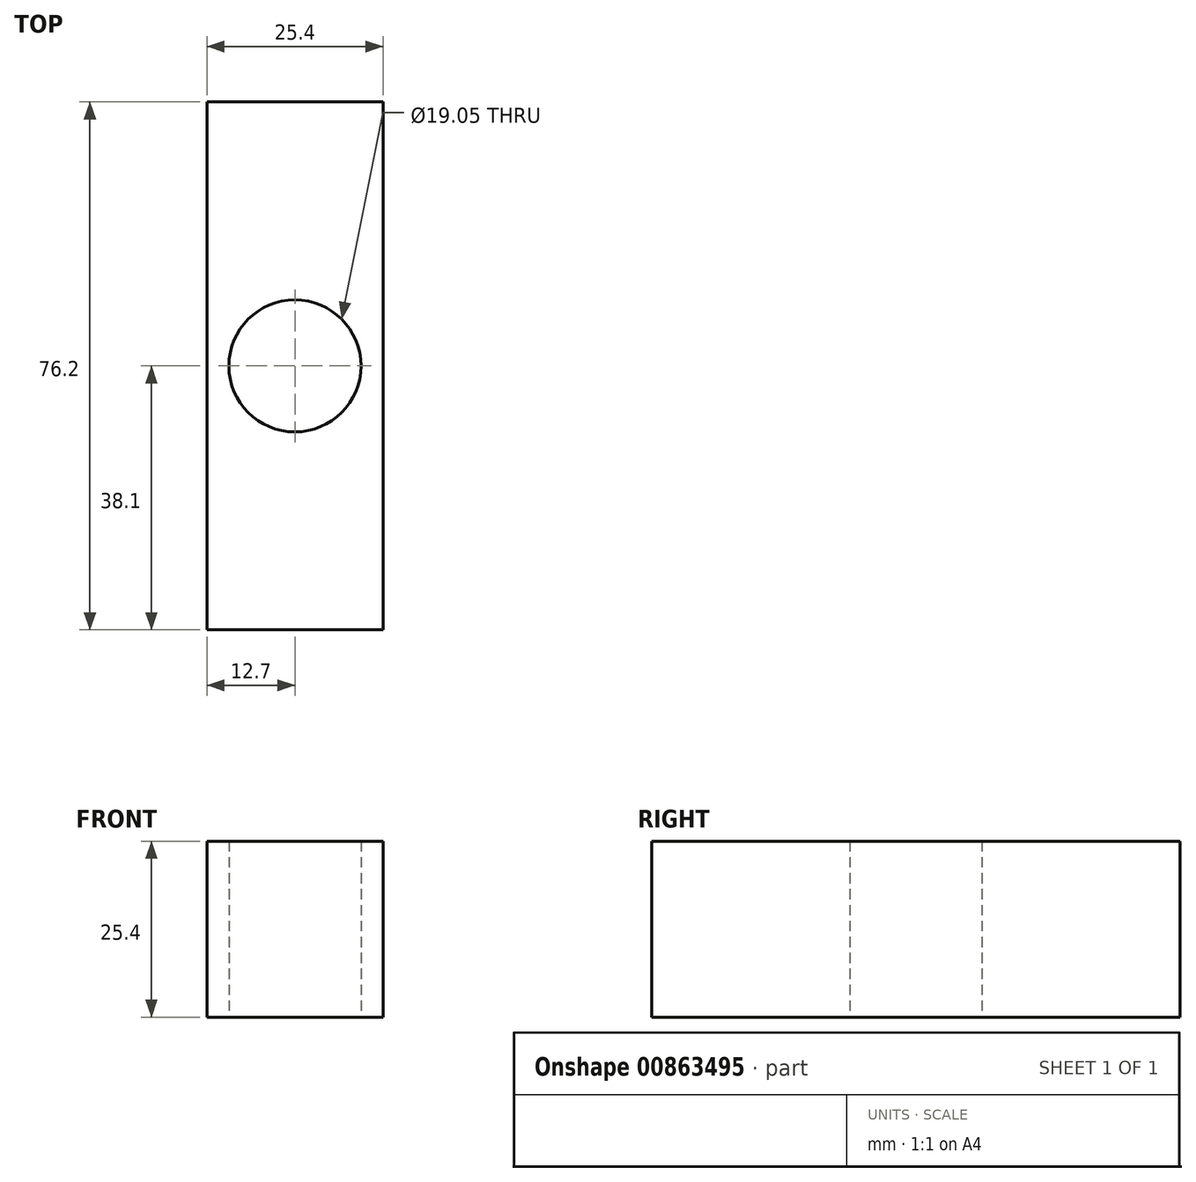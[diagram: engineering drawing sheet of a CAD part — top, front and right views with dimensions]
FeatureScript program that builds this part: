
annotation { "Feature Type Name" : "Feature", "Feature Type Description" : "" }
export const myFeature = defineFeature(function(context is Context, id is Id, definition is map)
    precondition{}
    {
        {
            var Q0;
            Q0=qCreatedBy(makeId("Top.planeOp"),FACE);
            var sketch = newSketch(context, id + "F0", { "sketchPlane" : qUnion([Q0])});
            skLineSegment(sketch, "E0.bottom", {"start": v(12.7, 38.1) * mm, "end": v(-12.7, 38.1) * mm});
            skLineSegment(sketch, "E0.top", {"start": v(12.7, -38.1) * mm, "end": v(-12.7, -38.1) * mm});
            skLineSegment(sketch, "E0.left", {"start": v(12.7, 38.1) * mm, "end": v(12.7, -38.1) * mm});
            skLineSegment(sketch, "E0.right", {"start": v(-12.7, 38.1) * mm, "end": v(-12.7, -38.1) * mm});
            skPoint(sketch, "E0.middle", {"position": v(0, 0) * mm});
            skCircle(sketch, "E1", {"center": v(0, 0) * mm, "radius": 9.53 * mm});
            skSolve(sketch);
        }
        {
            var Q0;
            Q0 = qSketchRegion(id + "F0", true);
            extrude(context, id + "F1", {"entities" : qUnion([Q0]), "depth" : 25.4 * mm, "offsetDistance" : 25.4 * mm});
        }
        {
            var Q0;
            Q0=qCreatedBy(makeId("Top.planeOp"),FACE);
            var sketch = newSketch(context, id + "F2", { "sketchPlane" : qUnion([Q0])});
            skCircle(sketch, "E2", {"center": v(0, 0) * mm, "radius": 9.53 * mm});
            skSolve(sketch);
        }
        {
            var Q0;
            Q0 = qSketchRegion(id + "F2", true);
            extrude(context, id + "F3", {"entities" : qUnion([Q0]), "depth" : 25.4 * mm, "offsetDistance" : 25.4 * mm});
        }
    });
